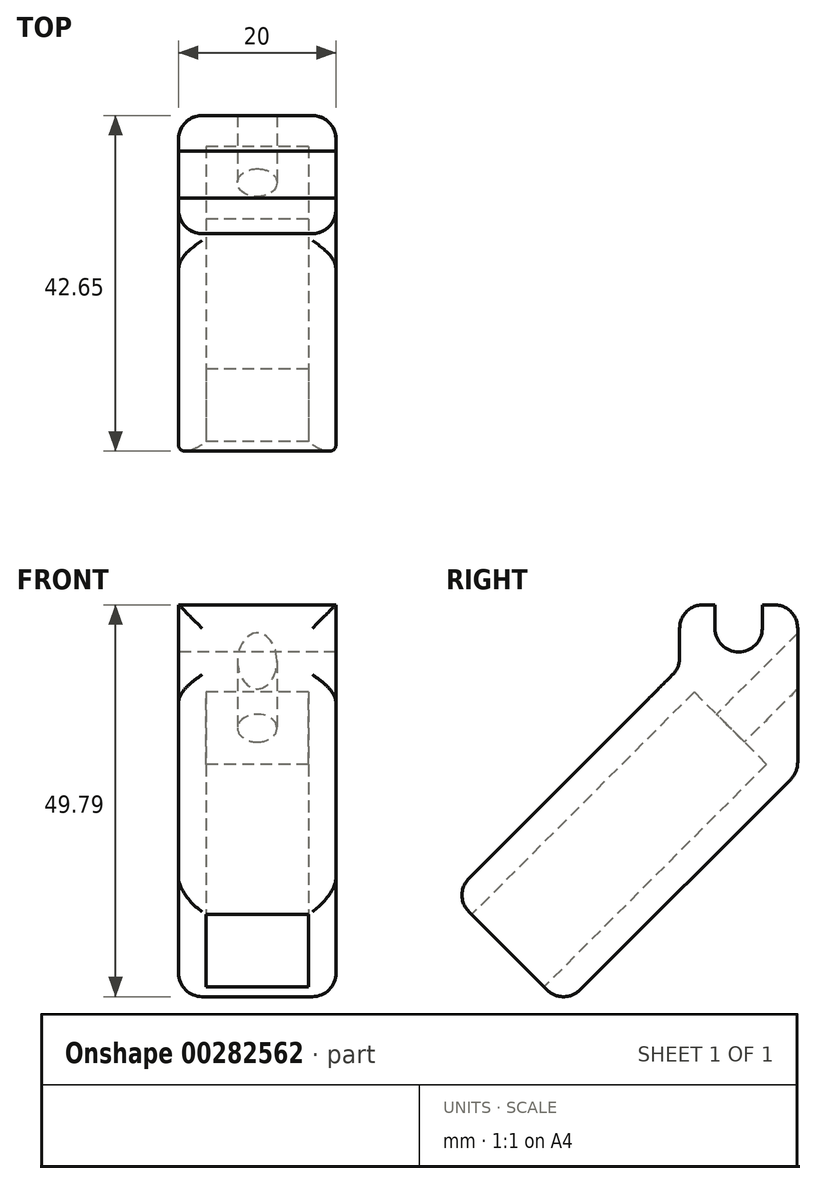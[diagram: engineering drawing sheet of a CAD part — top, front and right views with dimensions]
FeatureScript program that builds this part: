
annotation { "Feature Type Name" : "Feature", "Feature Type Description" : "" }
export const myFeature = defineFeature(function(context is Context, id is Id, definition is map)
    precondition{}
    {
        {
            var Q0;
            Q0=qCreatedBy(makeId("Right.planeOp"),FACE);
            var sketch = newSketch(context, id + "F0", { "sketchPlane" : qUnion([Q0])});
            skLineSegment(sketch, "E0", {"start": v(0, 0) * mm, "end": v(-15, 0) * mm});
            skLineSegment(sketch, "E1", {"start": v(-15, 0) * mm, "end": v(-15, -5) * mm});
            skLineSegment(sketch, "E2", {"start": v(-15, -5) * mm, "end": v(-43.9, -33.9) * mm});
            skLineSegment(sketch, "E3", {"start": v(-43.9, -33.9) * mm, "end": v(-29.75, -48.03) * mm});
            skLineSegment(sketch, "E4", {"start": v(-29.75, -48.03) * mm, "end": v(0, -18.28) * mm});
            skLineSegment(sketch, "E5", {"start": v(0, -18.28) * mm, "end": v(0, 0) * mm});
            skLineSegment(sketch, "E6", {"start": v(-40.36, -37.43) * mm, "end": v(-12.07, -9.14) * mm, "construction": true});
            skLineSegment(sketch, "E7", {"start": v(-12.07, -9.14) * mm, "end": v(-5, -16.21) * mm, "construction": true});
            skLineSegment(sketch, "E8", {"start": v(-5, -16.21) * mm, "end": v(-33.28, -44.5) * mm, "construction": true});
            skPoint(sketch, "E9", {"position": v(-7.5, 0) * mm});
            skLineSegment(sketch, "E10", {"start": v(-10.5, 0) * mm, "end": v(-10.5, 0) * mm});
            skArc(sketch, "E11", {"start": v(-4.5, 0) * mm, "mid": v(-7.5, 3) * mm, "end": v(-10.5, 0) * mm, "construction": true});
            skArc(sketch, "E12", {"start": v(-10.5, 0) * mm, "mid": v(-7.5, -3) * mm, "end": v(-4.5, 0) * mm});
            skSolve(sketch);
        }
        {
            var Q0;
            {var subQ0=sQuery(id+"F0.wireOp",EDGE,"E1");Q0=makeQuery(id+"F0.imprint","IMPRINT",FACE,{"disambiguationData":[TD([[makeQuery(id+"F0.imprint","IMPRINT",EDGE,{"derivedFrom":subQ0}),1.0]])]});}
            var Q1;
            {var subQ0=sQuery(id+"F0.wireOp",EDGE,"E2");Q1=makeQuery(id+"F0.imprint","IMPRINT",FACE,{"disambiguationData":[TD([[makeQuery(id+"F0.imprint","IMPRINT",EDGE,{"derivedFrom":subQ0}),1.0]])]});}
            extrude(context, id + "F1", {"entities" : qUnion([Q0, Q1]), "depth" : 20 * mm});
        }
        {
            var Q0;
            Q0=makeQuery(id+"F1.opExtrude","SWEPT_FACE",FACE,{"disambiguationData":[OSD([sQuery(id+"F0.wireOp",EDGE,"E3")])]});
            var sketch = newSketch(context, id + "F2", { "sketchPlane" : qUnion([Q0])});
            skPoint(sketch, "E13", {"position": v(10, -2.93) * mm});
            skPoint(sketch, "E13.positionSnap0", {"position": v(0, -2.93) * mm});
            skPoint(sketch, "E13.positionSnap1", {"position": v(10, 7.07) * mm});
            skLineSegment(sketch, "E14.bottom", {"start": v(16.5, -9.43) * mm, "end": v(3.5, -9.43) * mm});
            skLineSegment(sketch, "E14.top", {"start": v(16.5, 3.57) * mm, "end": v(3.5, 3.57) * mm});
            skLineSegment(sketch, "E14.left", {"start": v(16.5, -9.43) * mm, "end": v(16.5, 3.57) * mm});
            skLineSegment(sketch, "E14.right", {"start": v(3.5, -9.43) * mm, "end": v(3.5, 3.57) * mm});
            skSolve(sketch);
        }
        {
            var Q0;
            Q0=makeQuery(id+"F2.imprint","IMPRINT",FACE,{"disambiguationData":[TD([[makeQuery(id+"F2.imprint","IMPRINT",EDGE,{"derivedFrom":sQuery(id+"F2.wireOp",EDGE,"E14.bottom")}),-1.0]])]});
            extrude(context, id + "F3", {"entities" : qUnion([Q0]), "operationType" : NewBodyOperationType.REMOVE, "oppositeDirection" : true, "depth" : 40 * mm});
        }
        {
            var Q0;
            Q0=makeQuery(id+"F3.boolean.opBoolean","COPY",FACE,{"derivedFrom":makeQuery(id+"F3.opExtrude","CAP_FACE",FACE,{"disambiguationData":[OSD([sQuery(id+"F2.wireOp",EDGE,"E14.bottom"),sQuery(id+"F2.wireOp",EDGE,"E14.top"),sQuery(id+"F2.wireOp",EDGE,"E14.left"),sQuery(id+"F2.wireOp",EDGE,"E14.right")])],"isStart":false})});
            var sketch = newSketch(context, id + "F4", { "sketchPlane" : qUnion([Q0])});
            skPoint(sketch, "E15", {"position": v(10, -2.93) * mm});
            skPoint(sketch, "E15.positionSnap0", {"position": v(3.5, -2.93) * mm});
            skPoint(sketch, "E15.positionSnap1", {"position": v(10, 3.57) * mm});
            skCircle(sketch, "E16", {"center": v(10, -2.93) * mm, "radius": 2.5 * mm});
            skSolve(sketch);
        }
        {
            var Q0;
            Q0=makeQuery(id+"F4.imprint","IMPRINT",FACE,{"disambiguationData":[TD([[makeQuery(id+"F4.imprint","IMPRINT",EDGE,{"derivedFrom":sQuery(id+"F4.wireOp",EDGE,"E16")}),1.0]])]});
            var Q1;
            Q1=makeQuery(id+"F1.opExtrude","SWEPT_FACE",FACE,{"disambiguationData":[OSD([sQuery(id+"F0.wireOp",EDGE,"E5")])]});
            extrude(context, id + "F5", {"entities" : qUnion([Q0]), "operationType" : NewBodyOperationType.REMOVE, "endBound" : BoundingType.UP_TO_SURFACE, "oppositeDirection" : true, "endBoundEntityFace" : qUnion([Q1]), "depth" : 25 * mm});
        }
        {
            var Q0;
            Q0=makeQuery(id+"F1.opExtrude","SWEPT_EDGE",EDGE,{"disambiguationData":[OSD([sQuery(id+"F0.wireOp",EDGE,"E2"),sQuery(id+"F0.wireOp",EDGE,"E3")])]});
            var Q1;
            Q1=makeQuery(id+"F1.opExtrude","CAP_EDGE",EDGE,{"disambiguationData":[OSD([sQuery(id+"F0.wireOp",EDGE,"E3")])],"isStart":true});
            var Q2;
            Q2=makeQuery(id+"F1.opExtrude","SWEPT_EDGE",EDGE,{"disambiguationData":[OSD([sQuery(id+"F0.wireOp",EDGE,"E3"),sQuery(id+"F0.wireOp",EDGE,"E4")])]});
            var Q3;
            Q3=makeQuery(id+"F1.opExtrude","CAP_EDGE",EDGE,{"disambiguationData":[OSD([sQuery(id+"F0.wireOp",EDGE,"E3")])],"isStart":false});
            var Q4;
            Q4=makeQuery(id+"F1.opExtrude","SWEPT_EDGE",EDGE,{"disambiguationData":[OSD([sQuery(id+"F0.wireOp",EDGE,"E4"),sQuery(id+"F0.wireOp",EDGE,"E5")])]});
            var Q5;
            Q5=makeQuery(id+"F1.opExtrude","SWEPT_EDGE",EDGE,{"disambiguationData":[OSD([sQuery(id+"F0.wireOp",EDGE,"E1"),sQuery(id+"F0.wireOp",EDGE,"E2")])]});
            var Q6;
            Q6=makeQuery(id+"F1.opExtrude","CAP_EDGE",EDGE,{"disambiguationData":[OSD([sQuery(id+"F0.wireOp",EDGE,"E4")])],"isStart":false});
            var Q7;
            Q7=makeQuery(id+"F1.opExtrude","CAP_EDGE",EDGE,{"disambiguationData":[OSD([sQuery(id+"F0.wireOp",EDGE,"E5")])],"isStart":false});
            var Q8;
            Q8=makeQuery(id+"F1.opExtrude","CAP_EDGE",EDGE,{"disambiguationData":[OSD([sQuery(id+"F0.wireOp",EDGE,"E1")])],"isStart":false});
            var Q9;
            Q9=makeQuery(id+"F1.opExtrude","CAP_EDGE",EDGE,{"disambiguationData":[OSD([sQuery(id+"F0.wireOp",EDGE,"E1")])],"isStart":true});
            var Q10;
            Q10=makeQuery(id+"F1.opExtrude","CAP_EDGE",EDGE,{"disambiguationData":[OSD([sQuery(id+"F0.wireOp",EDGE,"E4")])],"isStart":true});
            var Q11;
            Q11=makeQuery(id+"F1.opExtrude","CAP_EDGE",EDGE,{"disambiguationData":[OSD([sQuery(id+"F0.wireOp",EDGE,"E5")])],"isStart":true});
            fillet(context, id + "F6", {"entities" : qUnion([Q0, Q1, Q2, Q3, Q4, Q5, Q6, Q7, Q8, Q9, Q10, Q11]), "radius" : 3 * mm, "tangentPropagation" : true, "allowEdgeOverflow" : false});
        }
        {
            var Q0;
            {var subQ0=sQuery(id+"F0.wireOp",EDGE,"E0");Q0=makeQuery(id+"F1.opExtrude","SWEPT_FACE",FACE,{"disambiguationData":[OSD([subQ0]),TDD([makeQuery(id+"F0.imprint","IMPRINT",EDGE,{"disambiguationData":[TD([[makeQuery(id+"F0.imprint","INTERSECT",VERTEX,{"derivedFrom":[subQ0,sQuery(id+"F0.wireOp",EDGE,"E5")]}),-1.0]])],"derivedFrom":subQ0})])]});}
            var Q1;
            {var subQ0=sQuery(id+"F0.wireOp",EDGE,"E0");Q1=makeQuery(id+"F1.opExtrude","SWEPT_FACE",FACE,{"disambiguationData":[OSD([subQ0]),TDD([makeQuery(id+"F0.imprint","IMPRINT",EDGE,{"disambiguationData":[TD([[makeQuery(id+"F0.imprint","INTERSECT",VERTEX,{"derivedFrom":[subQ0,sQuery(id+"F0.wireOp",EDGE,"E1")]}),1.0]])],"derivedFrom":subQ0})])]});}
            extrude(context, id + "F7", {"entities" : qUnion([Q0, Q1]), "operationType" : NewBodyOperationType.ADD, "depth" : 3 * mm});
        }
        {
            var Q0;
            {var subQ0=sQuery(id+"F0.wireOp",EDGE,"E1");var subQ1=sQuery(id+"F0.wireOp",EDGE,"E0");Q0=makeQuery(id+"F7.opExtrude","CAP_EDGE",EDGE,{"disambiguationData":[OSD([subQ1,subQ0]),TDD([makeQuery(id+"F1.opExtrude","SWEPT_EDGE",EDGE,{"disambiguationData":[OSD([subQ1,subQ0])]})])],"isStart":false});}
            var Q1;
            {var subQ0=sQuery(id+"F0.wireOp",EDGE,"E5");var subQ1=sQuery(id+"F0.wireOp",EDGE,"E0");Q1=makeQuery(id+"F7.opExtrude","CAP_EDGE",EDGE,{"disambiguationData":[OSD([subQ1,subQ0]),TDD([makeQuery(id+"F1.opExtrude","SWEPT_EDGE",EDGE,{"disambiguationData":[OSD([subQ1,subQ0])]})])],"isStart":false});}
            fillet(context, id + "F8", {"entities" : qUnion([Q0, Q1]), "radius" : 3 * mm, "allowEdgeOverflow" : false});
        }
    });
